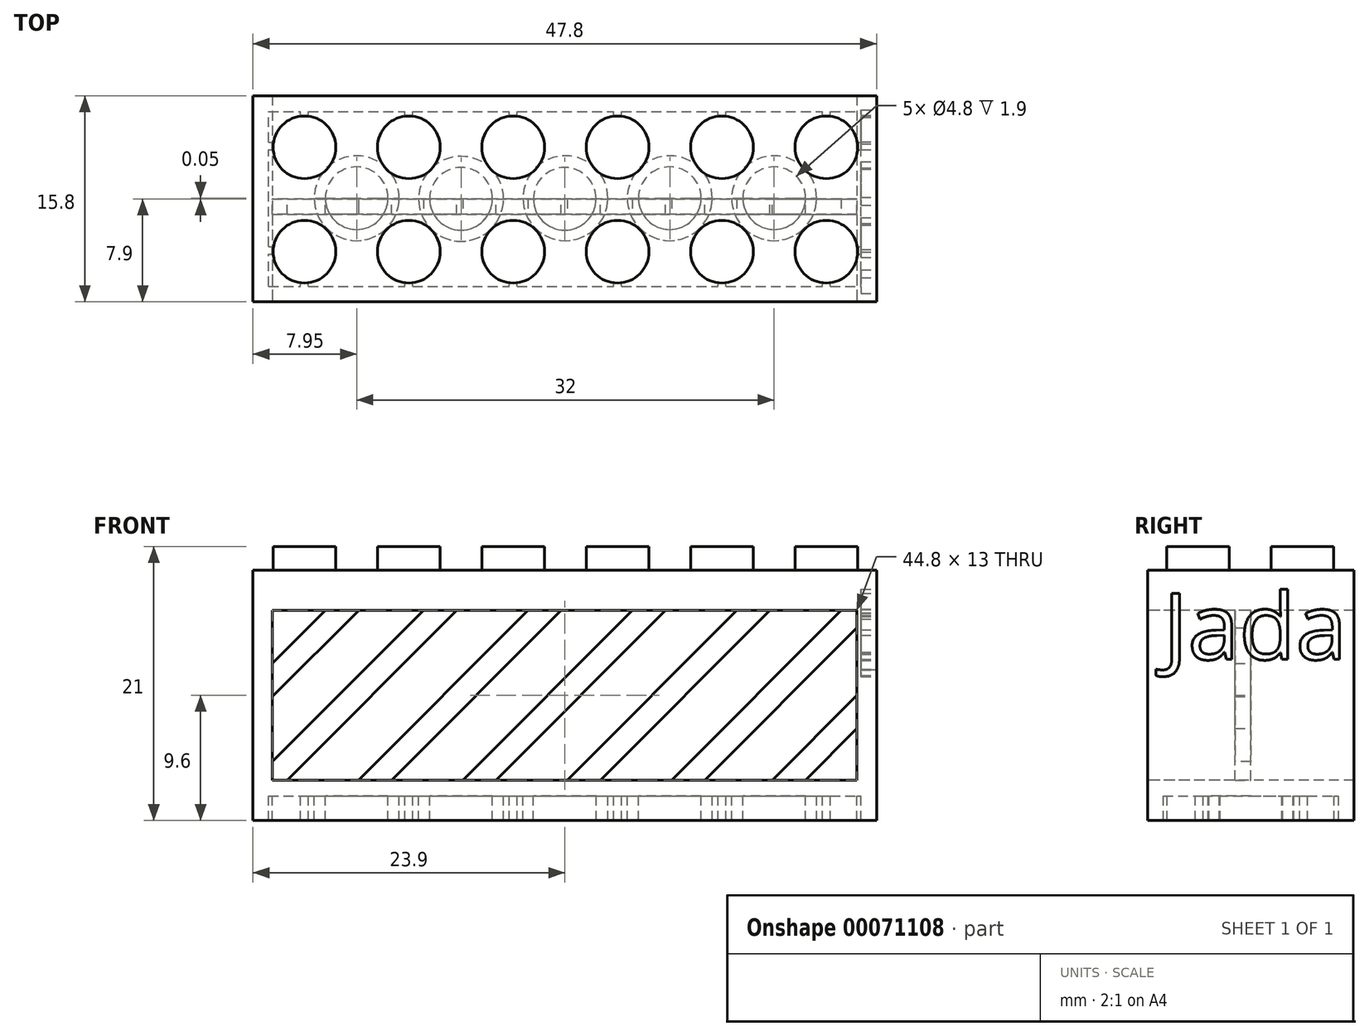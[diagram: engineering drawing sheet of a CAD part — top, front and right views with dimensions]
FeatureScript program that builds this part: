
annotation { "Feature Type Name" : "Feature", "Feature Type Description" : "" }
export const myFeature = defineFeature(function(context is Context, id is Id, definition is map)
    precondition{}
    {
        {
            var Q0;
            Q0=qCreatedBy(makeId("Top.planeOp"),FACE);
            var sketch = newSketch(context, id + "F0", { "sketchPlane" : qUnion([Q0])});
            skLineSegment(sketch, "E0.rect.bottom", {"start": v(-23.9, -7.9) * mm, "end": v(23.9, -7.9) * mm});
            skLineSegment(sketch, "E0.rect.top", {"start": v(-23.9, 7.9) * mm, "end": v(23.9, 7.9) * mm});
            skLineSegment(sketch, "E0.rect.left", {"start": v(-23.9, -7.9) * mm, "end": v(-23.9, 7.9) * mm});
            skLineSegment(sketch, "E0.rect.right", {"start": v(23.9, -7.9) * mm, "end": v(23.9, 7.9) * mm});
            skPoint(sketch, "E0.rect.middle", {"position": v(0, 0) * mm});
            skSolve(sketch);
        }
        {
            var Q0;
            Q0 = qSketchRegion(id + "F0", true);
            extrude(context, id + "F1", {"entities" : qUnion([Q0]), "depth" : 19.2 * mm});
        }
        {
            var Q0;
            Q0=makeQuery(id+"F1.opExtrude","CAP_FACE",FACE,{"disambiguationData":[OSD([sQuery(id+"F0.wireOp",EDGE,"E0.rect.bottom"),sQuery(id+"F0.wireOp",EDGE,"E0.rect.top"),sQuery(id+"F0.wireOp",EDGE,"E0.rect.left"),sQuery(id+"F0.wireOp",EDGE,"E0.rect.right")])],"isStart":true});
            var sketch = newSketch(context, id + "F2", { "sketchPlane" : qUnion([Q0])});
            skLineSegment(sketch, "E1.bottom", {"start": v(-22.7, 6.7) * mm, "end": v(22.7, 6.7) * mm});
            skLineSegment(sketch, "E1.top", {"start": v(-22.7, -6.7) * mm, "end": v(22.7, -6.7) * mm});
            skLineSegment(sketch, "E1.left", {"start": v(-22.7, 6.7) * mm, "end": v(-22.7, -6.7) * mm});
            skLineSegment(sketch, "E1.right", {"start": v(22.7, 6.7) * mm, "end": v(22.7, -6.7) * mm});
            skSolve(sketch);
        }
        {
            var Q0;
            Q0 = qSketchRegion(id + "F2", true);
            var Q1;
            Q1=makeQuery(id+"F2.imprint","IMPRINT",FACE,{"disambiguationData":[TD([[makeQuery(id+"F2.imprint","IMPRINT",EDGE,{"derivedFrom":sQuery(id+"F2.wireOp",EDGE,"E1.bottom")}),-1.0]])]});
            extrude(context, id + "F3", {"entities" : qUnion([Q0, Q1]), "operationType" : NewBodyOperationType.REMOVE, "oppositeDirection" : true, "depth" : 1.9 * mm});
        }
        {
            var Q0;
            Q0=makeQuery(id+"F1.opExtrude","SWEPT_FACE",FACE,{"disambiguationData":[OSD([sQuery(id+"F0.wireOp",EDGE,"E0.rect.bottom")])]});
            var sketch = newSketch(context, id + "F4", { "sketchPlane" : qUnion([Q0])});
            skLineSegment(sketch, "E2.bottom", {"start": v(-22.4, 16.1) * mm, "end": v(22.4, 16.1) * mm});
            skLineSegment(sketch, "E2.top", {"start": v(-22.4, 3.1) * mm, "end": v(22.4, 3.1) * mm});
            skLineSegment(sketch, "E2.left", {"start": v(-22.4, 16.1) * mm, "end": v(-22.4, 3.1) * mm});
            skLineSegment(sketch, "E2.right", {"start": v(22.4, 16.1) * mm, "end": v(22.4, 3.1) * mm});
            skSolve(sketch);
        }
        {
            var Q0;
            Q0=makeQuery(id+"F4.imprint","IMPRINT",FACE,{"disambiguationData":[TD([[makeQuery(id+"F4.imprint","IMPRINT",EDGE,{"derivedFrom":sQuery(id+"F4.wireOp",EDGE,"E2.bottom")}),-1.0]])]});
            extrude(context, id + "F5", {"entities" : qUnion([Q0]), "operationType" : NewBodyOperationType.REMOVE, "oppositeDirection" : true, "depth" : 15.8 * mm});
        }
        {
            var Q0;
            Q0=qCreatedBy(makeId("Front.planeOp"),FACE);
            var sketch = newSketch(context, id + "F6", { "sketchPlane" : qUnion([Q0])});
            skLineSegment(sketch, "E3", {"start": v(-23.8, 10.64) * mm, "end": v(-15.32, 19.12) * mm});
            skLineSegment(sketch, "E4", {"start": v(18.06, 2.72) * mm, "end": v(23.58, 8.24) * mm});
            skLineSegment(sketch, "E5", {"start": v(-23.7, 8.18) * mm, "end": v(-13.08, 18.81) * mm});
            skLineSegment(sketch, "E6", {"start": v(15.51, 2.72) * mm, "end": v(23.81, 11.02) * mm});
            skPoint(sketch, "E7", {"position": v(-15.8, 16.1) * mm});
            skPoint(sketch, "E8", {"position": v(22.4, 9.6) * mm});
            skLineSegment(sketch, "E9", {"start": v(-9.13, 17.8) * mm, "end": v(-22.8, 4.12) * mm});
            skLineSegment(sketch, "E10", {"start": v(-21.76, 2.62) * mm, "end": v(-6.76, 17.61) * mm});
            skLineSegment(sketch, "E11", {"start": v(-9.13, 17.8) * mm, "end": v(-6.76, 17.61) * mm});
            skLineSegment(sketch, "E12", {"start": v(-23.03, 2.62) * mm, "end": v(-21.76, 2.62) * mm});
            skLineSegment(sketch, "E13", {"start": v(-23.7, 8.18) * mm, "end": v(-23.8, 10.64) * mm});
            skLineSegment(sketch, "E14", {"start": v(-15.32, 19.12) * mm, "end": v(-13.08, 18.81) * mm});
            skLineSegment(sketch, "E15", {"start": v(23.58, 8.24) * mm, "end": v(23.81, 11.02) * mm});
            skLineSegment(sketch, "E16.1.0.0", {"start": v(-1.13, 17.8) * mm, "end": v(-14.8, 4.12) * mm});
            skLineSegment(sketch, "E16.1.0.1", {"start": v(-1.13, 17.8) * mm, "end": v(1.24, 17.61) * mm});
            skLineSegment(sketch, "E16.1.0.2", {"start": v(-13.76, 2.62) * mm, "end": v(1.24, 17.61) * mm});
            skLineSegment(sketch, "E16.1.0.3", {"start": v(-16.3, 2.62) * mm, "end": v(-13.76, 2.62) * mm});
            skLineSegment(sketch, "E16.1.0.4", {"start": v(-14.8, 4.12) * mm, "end": v(-16.3, 2.62) * mm});
            skLineSegment(sketch, "E16.2.0.0", {"start": v(6.87, 17.8) * mm, "end": v(-6.8, 4.12) * mm});
            skLineSegment(sketch, "E16.2.0.1", {"start": v(6.87, 17.8) * mm, "end": v(9.24, 17.61) * mm});
            skLineSegment(sketch, "E16.2.0.2", {"start": v(-5.76, 2.62) * mm, "end": v(9.24, 17.61) * mm});
            skLineSegment(sketch, "E16.2.0.3", {"start": v(-8.3, 2.62) * mm, "end": v(-5.76, 2.62) * mm});
            skLineSegment(sketch, "E16.2.0.4", {"start": v(-6.8, 4.12) * mm, "end": v(-8.3, 2.62) * mm});
            skLineSegment(sketch, "E16.3.0.0", {"start": v(14.87, 17.8) * mm, "end": v(1.2, 4.12) * mm});
            skLineSegment(sketch, "E16.3.0.1", {"start": v(14.87, 17.8) * mm, "end": v(17.24, 17.61) * mm});
            skLineSegment(sketch, "E16.3.0.2", {"start": v(2.24, 2.62) * mm, "end": v(17.24, 17.61) * mm});
            skLineSegment(sketch, "E16.3.0.3", {"start": v(-0.3, 2.62) * mm, "end": v(2.24, 2.62) * mm});
            skLineSegment(sketch, "E16.3.0.4", {"start": v(1.2, 4.12) * mm, "end": v(-0.3, 2.62) * mm});
            skLineSegment(sketch, "E16.4.0.0", {"start": v(22.87, 17.8) * mm, "end": v(9.2, 4.12) * mm});
            skLineSegment(sketch, "E16.4.0.2", {"start": v(10.24, 2.62) * mm, "end": v(23.25, 15.63) * mm});
            skLineSegment(sketch, "E16.4.0.3", {"start": v(7.7, 2.62) * mm, "end": v(10.24, 2.62) * mm});
            skLineSegment(sketch, "E16.4.0.4", {"start": v(9.2, 4.12) * mm, "end": v(7.7, 2.62) * mm});
            skLineSegment(sketch, "E16.direction1", {"start": v(-22.8, 4.12) * mm, "end": v(-14.8, 4.12) * mm, "construction": true});
            skLineSegment(sketch, "E17", {"start": v(-23.03, 2.62) * mm, "end": v(-22.8, 4.12) * mm});
            skLineSegment(sketch, "E18", {"start": v(22.87, 17.8) * mm, "end": v(23.25, 15.63) * mm});
            skLineSegment(sketch, "E19", {"start": v(15.51, 2.72) * mm, "end": v(18.06, 2.72) * mm});
            skPoint(sketch, "E20.start.orphan", {"position": v(12.8, 0) * mm});
            skPoint(sketch, "E21.orphan", {"position": v(15.34, 0) * mm});
            skSolve(sketch);
        }
        {
            var Q0;
            Q0 = qSketchRegion(id + "F6", true);
            extrude(context, id + "F7", {"entities" : qUnion([Q0]), "operationType" : NewBodyOperationType.ADD, "depth" : 1.2 * mm});
        }
        {
            var Q0;
            Q0=makeQuery(id+"F1.opExtrude","CAP_FACE",FACE,{"disambiguationData":[OSD([sQuery(id+"F0.wireOp",EDGE,"E0.rect.bottom"),sQuery(id+"F0.wireOp",EDGE,"E0.rect.top"),sQuery(id+"F0.wireOp",EDGE,"E0.rect.left"),sQuery(id+"F0.wireOp",EDGE,"E0.rect.right")])],"isStart":false});
            var sketch = newSketch(context, id + "F8", { "sketchPlane" : qUnion([Q0])});
            skCircle(sketch, "E22", {"center": v(-19.95, 3.95) * mm, "radius": 2.4 * mm});
            skCircle(sketch, "E23.0.1.0", {"center": v(-19.95, -4.05) * mm, "radius": 2.4 * mm});
            skCircle(sketch, "E23.1.0.0", {"center": v(-11.95, 3.95) * mm, "radius": 2.4 * mm});
            skCircle(sketch, "E23.1.1.0", {"center": v(-11.95, -4.05) * mm, "radius": 2.4 * mm});
            skCircle(sketch, "E23.2.0.0", {"center": v(-3.95, 3.95) * mm, "radius": 2.4 * mm});
            skCircle(sketch, "E23.2.1.0", {"center": v(-3.95, -4.05) * mm, "radius": 2.4 * mm});
            skCircle(sketch, "E23.3.0.0", {"center": v(4.05, 3.95) * mm, "radius": 2.4 * mm});
            skCircle(sketch, "E23.3.1.0", {"center": v(4.05, -4.05) * mm, "radius": 2.4 * mm});
            skCircle(sketch, "E23.4.0.0", {"center": v(12.05, 3.95) * mm, "radius": 2.4 * mm});
            skCircle(sketch, "E23.4.1.0", {"center": v(12.05, -4.05) * mm, "radius": 2.4 * mm});
            skCircle(sketch, "E23.5.0.0", {"center": v(20.05, 3.95) * mm, "radius": 2.4 * mm});
            skCircle(sketch, "E23.5.1.0", {"center": v(20.05, -4.05) * mm, "radius": 2.4 * mm});
            skLineSegment(sketch, "E23.direction1", {"start": v(-19.95, 3.95) * mm, "end": v(-11.95, 3.95) * mm, "construction": true});
            skLineSegment(sketch, "E23.direction2", {"start": v(-19.95, 3.95) * mm, "end": v(-19.95, -4.05) * mm, "construction": true});
            skSolve(sketch);
        }
        {
            var Q0;
            Q0 = qSketchRegion(id + "F8", true);
            extrude(context, id + "F9", {"entities" : qUnion([Q0]), "operationType" : NewBodyOperationType.ADD, "depth" : 1.8 * mm});
        }
        {
            var Q0;
            Q0=makeQuery(id+"F3.boolean.opBoolean","COPY",FACE,{"derivedFrom":makeQuery(id+"F3.opExtrude","CAP_FACE",FACE,{"disambiguationData":[OSD([sQuery(id+"F2.wireOp",EDGE,"E1.bottom"),sQuery(id+"F2.wireOp",EDGE,"E1.top"),sQuery(id+"F2.wireOp",EDGE,"E1.left"),sQuery(id+"F2.wireOp",EDGE,"E1.right")])],"isStart":false})});
            var sketch = newSketch(context, id + "F10", { "sketchPlane" : qUnion([Q0])});
            skCircle(sketch, "E24", {"center": v(-19.95, 3.95) * mm, "radius": 1.3 * mm, "construction": true});
            skCircle(sketch, "E25.0.1.0", {"center": v(-19.95, -4.05) * mm, "radius": 1.3 * mm, "construction": true});
            skCircle(sketch, "E25.1.0.0", {"center": v(-11.95, 3.95) * mm, "radius": 1.3 * mm, "construction": true});
            skCircle(sketch, "E25.1.1.0", {"center": v(-11.95, -4.05) * mm, "radius": 1.3 * mm, "construction": true});
            skCircle(sketch, "E25.2.0.0", {"center": v(-3.95, 3.95) * mm, "radius": 1.3 * mm, "construction": true});
            skCircle(sketch, "E25.2.1.0", {"center": v(-3.95, -4.05) * mm, "radius": 1.3 * mm, "construction": true});
            skCircle(sketch, "E25.3.0.0", {"center": v(4.05, 3.95) * mm, "radius": 1.3 * mm, "construction": true});
            skCircle(sketch, "E25.3.1.0", {"center": v(4.05, -4.05) * mm, "radius": 1.3 * mm, "construction": true});
            skCircle(sketch, "E25.4.0.0", {"center": v(12.05, 3.95) * mm, "radius": 1.3 * mm, "construction": true});
            skCircle(sketch, "E25.4.1.0", {"center": v(12.05, -4.05) * mm, "radius": 1.3 * mm, "construction": true});
            skCircle(sketch, "E25.5.0.0", {"center": v(20.05, 3.95) * mm, "radius": 1.3 * mm, "construction": true});
            skCircle(sketch, "E25.5.1.0", {"center": v(20.05, -4.05) * mm, "radius": 1.3 * mm, "construction": true});
            skLineSegment(sketch, "E25.direction1", {"start": v(-19.95, 3.95) * mm, "end": v(-11.95, 3.95) * mm, "construction": true});
            skLineSegment(sketch, "E25.direction2", {"start": v(-19.95, 3.95) * mm, "end": v(-19.95, -4.05) * mm, "construction": true});
            skLineSegment(sketch, "E26", {"start": v(-11.95, 3.95) * mm, "end": v(-19.95, -4.05) * mm, "construction": true});
            skLineSegment(sketch, "E27", {"start": v(-11.95, 3.95) * mm, "end": v(-3.95, -4.05) * mm, "construction": true});
            skLineSegment(sketch, "E28", {"start": v(4.05, 3.95) * mm, "end": v(-3.95, -4.05) * mm, "construction": true});
            skLineSegment(sketch, "E29", {"start": v(4.05, 3.95) * mm, "end": v(12.05, -4.05) * mm, "construction": true});
            skLineSegment(sketch, "E30", {"start": v(20.05, 3.95) * mm, "end": v(12.05, -4.05) * mm, "construction": true});
            skLineSegment(sketch, "E31", {"start": v(20.05, -4.05) * mm, "end": v(12.05, 3.95) * mm, "construction": true});
            skLineSegment(sketch, "E32", {"start": v(12.05, 3.95) * mm, "end": v(4.05, -4.05) * mm, "construction": true});
            skLineSegment(sketch, "E33", {"start": v(4.05, -4.05) * mm, "end": v(-3.95, 3.95) * mm, "construction": true});
            skLineSegment(sketch, "E34", {"start": v(-3.95, 3.95) * mm, "end": v(-11.95, -4.05) * mm, "construction": true});
            skLineSegment(sketch, "E35", {"start": v(-11.95, -4.05) * mm, "end": v(-19.95, 3.95) * mm, "construction": true});
            skPoint(sketch, "E36", {"position": v(8.05, -0.05) * mm});
            skPoint(sketch, "E37", {"position": v(16.05, -0.05) * mm});
            skPoint(sketch, "E38", {"position": v(0.05, -0.05) * mm});
            skPoint(sketch, "E39", {"position": v(-7.95, 0) * mm});
            skPoint(sketch, "E39.positionSnap0", {"position": v(-7.95, -0.05) * mm});
            skPoint(sketch, "E40", {"position": v(-15.95, -0.05) * mm});
            skCircle(sketch, "E41", {"center": v(16.05, -0.05) * mm, "radius": 3.25 * mm});
            skCircle(sketch, "E42", {"center": v(8.05, -0.05) * mm, "radius": 3.25 * mm});
            skCircle(sketch, "E43", {"center": v(0.05, -0.05) * mm, "radius": 3.25 * mm});
            skCircle(sketch, "E44", {"center": v(-7.95, 0) * mm, "radius": 3.25 * mm});
            skCircle(sketch, "E45", {"center": v(-15.95, -0.05) * mm, "radius": 3.25 * mm});
            skCircle(sketch, "E46", {"center": v(16.05, -0.05) * mm, "radius": 2.4 * mm});
            skCircle(sketch, "E47", {"center": v(8.05, -0.05) * mm, "radius": 2.4 * mm});
            skCircle(sketch, "E48", {"center": v(0, 0) * mm, "radius": 2.4 * mm});
            skCircle(sketch, "E49", {"center": v(-7.95, 0) * mm, "radius": 2.4 * mm});
            skCircle(sketch, "E50", {"center": v(-15.95, -0.05) * mm, "radius": 2.4 * mm});
            skSolve(sketch);
        }
        {
            var Q0;
            Q0 = qSketchRegion(id + "F10", true);
            var Q1;
            Q1=makeQuery(id+"F1.opExtrude","CAP_FACE",FACE,{"disambiguationData":[OSD([sQuery(id+"F0.wireOp",EDGE,"E0.rect.bottom"),sQuery(id+"F0.wireOp",EDGE,"E0.rect.top"),sQuery(id+"F0.wireOp",EDGE,"E0.rect.left"),sQuery(id+"F0.wireOp",EDGE,"E0.rect.right")])],"isStart":true});
            extrude(context, id + "F11", {"entities" : qUnion([Q0]), "operationType" : NewBodyOperationType.ADD, "endBound" : BoundingType.UP_TO_SURFACE, "endBoundEntityFace" : qUnion([Q1]), "depth" : 25 * mm});
        }
        {
            var Q0;
            {var subQ0=sQuery(id+"F2.wireOp",EDGE,"E1.right");var subQ1=sQuery(id+"F2.wireOp",EDGE,"E1.left");var subQ2=sQuery(id+"F2.wireOp",EDGE,"E1.top");var subQ3=sQuery(id+"F2.wireOp",EDGE,"E1.bottom");Q0=makeQuery(id+"F11.boolean.opBoolean","SPLIT",FACE,{"disambiguationData":[TD([makeQuery(id+"F3.boolean.opBoolean","COPY",FACE,{"derivedFrom":makeQuery(id+"F3.opExtrude","SWEPT_FACE",FACE,{"disambiguationData":[OSD([subQ3])]})})])],"derivedFrom":makeQuery(id+"F3.boolean.opBoolean","COPY",FACE,{"derivedFrom":makeQuery(id+"F3.opExtrude","CAP_FACE",FACE,{"disambiguationData":[OSD([subQ3,subQ2,subQ1,subQ0])],"isStart":false})})});}
            var sketch = newSketch(context, id + "F12", { "sketchPlane" : qUnion([Q0])});
            skLineSegment(sketch, "E51", {"start": v(-19.95, -4.05) * mm, "end": v(-19.95, 13.37) * mm, "construction": true});
            skLineSegment(sketch, "E52.bottom", {"start": v(-20.25, 6.7) * mm, "end": v(-19.65, 6.7) * mm});
            skLineSegment(sketch, "E52.top", {"start": v(-20.25, 6.4) * mm, "end": v(-19.65, 6.4) * mm});
            skLineSegment(sketch, "E52.left", {"start": v(-20.25, 6.7) * mm, "end": v(-20.25, 6.4) * mm});
            skLineSegment(sketch, "E52.right", {"start": v(-19.65, 6.7) * mm, "end": v(-19.65, 6.4) * mm});
            skLineSegment(sketch, "E53.0.1.0", {"start": v(-19.65, -6.4) * mm, "end": v(-19.65, -6.7) * mm});
            skLineSegment(sketch, "E53.0.1.1", {"start": v(-20.25, -6.7) * mm, "end": v(-19.65, -6.7) * mm});
            skLineSegment(sketch, "E53.0.1.2", {"start": v(-20.25, -6.4) * mm, "end": v(-20.25, -6.7) * mm});
            skLineSegment(sketch, "E53.0.1.3", {"start": v(-20.25, -6.4) * mm, "end": v(-19.65, -6.4) * mm});
            skLineSegment(sketch, "E53.1.0.0", {"start": v(-11.65, 6.7) * mm, "end": v(-11.65, 6.4) * mm});
            skLineSegment(sketch, "E53.1.0.1", {"start": v(-12.25, 6.4) * mm, "end": v(-11.65, 6.4) * mm});
            skLineSegment(sketch, "E53.1.0.2", {"start": v(-12.25, 6.7) * mm, "end": v(-12.25, 6.4) * mm});
            skLineSegment(sketch, "E53.1.0.3", {"start": v(-12.25, 6.7) * mm, "end": v(-11.65, 6.7) * mm});
            skLineSegment(sketch, "E53.1.1.0", {"start": v(-11.65, -6.4) * mm, "end": v(-11.65, -6.7) * mm});
            skLineSegment(sketch, "E53.1.1.1", {"start": v(-12.25, -6.7) * mm, "end": v(-11.65, -6.7) * mm});
            skLineSegment(sketch, "E53.1.1.2", {"start": v(-12.25, -6.4) * mm, "end": v(-12.25, -6.7) * mm});
            skLineSegment(sketch, "E53.1.1.3", {"start": v(-12.25, -6.4) * mm, "end": v(-11.65, -6.4) * mm});
            skLineSegment(sketch, "E53.2.0.0", {"start": v(-3.65, 6.7) * mm, "end": v(-3.65, 6.4) * mm});
            skLineSegment(sketch, "E53.2.0.1", {"start": v(-4.25, 6.4) * mm, "end": v(-3.65, 6.4) * mm});
            skLineSegment(sketch, "E53.2.0.2", {"start": v(-4.25, 6.7) * mm, "end": v(-4.25, 6.4) * mm});
            skLineSegment(sketch, "E53.2.0.3", {"start": v(-4.25, 6.7) * mm, "end": v(-3.65, 6.7) * mm});
            skLineSegment(sketch, "E53.2.1.0", {"start": v(-3.65, -6.4) * mm, "end": v(-3.65, -6.7) * mm});
            skLineSegment(sketch, "E53.2.1.1", {"start": v(-4.25, -6.7) * mm, "end": v(-3.65, -6.7) * mm});
            skLineSegment(sketch, "E53.2.1.2", {"start": v(-4.25, -6.4) * mm, "end": v(-4.25, -6.7) * mm});
            skLineSegment(sketch, "E53.2.1.3", {"start": v(-4.25, -6.4) * mm, "end": v(-3.65, -6.4) * mm});
            skLineSegment(sketch, "E53.3.0.0", {"start": v(4.35, 6.7) * mm, "end": v(4.35, 6.4) * mm});
            skLineSegment(sketch, "E53.3.0.1", {"start": v(3.75, 6.4) * mm, "end": v(4.35, 6.4) * mm});
            skLineSegment(sketch, "E53.3.0.2", {"start": v(3.75, 6.7) * mm, "end": v(3.75, 6.4) * mm});
            skLineSegment(sketch, "E53.3.0.3", {"start": v(3.75, 6.7) * mm, "end": v(4.35, 6.7) * mm});
            skLineSegment(sketch, "E53.3.1.0", {"start": v(4.35, -6.4) * mm, "end": v(4.35, -6.7) * mm});
            skLineSegment(sketch, "E53.3.1.1", {"start": v(3.75, -6.7) * mm, "end": v(4.35, -6.7) * mm});
            skLineSegment(sketch, "E53.3.1.2", {"start": v(3.75, -6.4) * mm, "end": v(3.75, -6.7) * mm});
            skLineSegment(sketch, "E53.3.1.3", {"start": v(3.75, -6.4) * mm, "end": v(4.35, -6.4) * mm});
            skLineSegment(sketch, "E53.4.0.0", {"start": v(12.35, 6.7) * mm, "end": v(12.35, 6.4) * mm});
            skLineSegment(sketch, "E53.4.0.1", {"start": v(11.75, 6.4) * mm, "end": v(12.35, 6.4) * mm});
            skLineSegment(sketch, "E53.4.0.2", {"start": v(11.75, 6.7) * mm, "end": v(11.75, 6.4) * mm});
            skLineSegment(sketch, "E53.4.0.3", {"start": v(11.75, 6.7) * mm, "end": v(12.35, 6.7) * mm});
            skLineSegment(sketch, "E53.4.1.0", {"start": v(12.35, -6.4) * mm, "end": v(12.35, -6.7) * mm});
            skLineSegment(sketch, "E53.4.1.1", {"start": v(11.75, -6.7) * mm, "end": v(12.35, -6.7) * mm});
            skLineSegment(sketch, "E53.4.1.2", {"start": v(11.75, -6.4) * mm, "end": v(11.75, -6.7) * mm});
            skLineSegment(sketch, "E53.4.1.3", {"start": v(11.75, -6.4) * mm, "end": v(12.35, -6.4) * mm});
            skLineSegment(sketch, "E53.5.0.0", {"start": v(20.35, 6.7) * mm, "end": v(20.35, 6.4) * mm});
            skLineSegment(sketch, "E53.5.0.1", {"start": v(19.75, 6.4) * mm, "end": v(20.35, 6.4) * mm});
            skLineSegment(sketch, "E53.5.0.2", {"start": v(19.75, 6.7) * mm, "end": v(19.75, 6.4) * mm});
            skLineSegment(sketch, "E53.5.0.3", {"start": v(19.75, 6.7) * mm, "end": v(20.35, 6.7) * mm});
            skLineSegment(sketch, "E53.5.1.0", {"start": v(20.35, -6.4) * mm, "end": v(20.35, -6.7) * mm});
            skLineSegment(sketch, "E53.5.1.1", {"start": v(19.75, -6.7) * mm, "end": v(20.35, -6.7) * mm});
            skLineSegment(sketch, "E53.5.1.2", {"start": v(19.75, -6.4) * mm, "end": v(19.75, -6.7) * mm});
            skLineSegment(sketch, "E53.5.1.3", {"start": v(19.75, -6.4) * mm, "end": v(20.35, -6.4) * mm});
            skLineSegment(sketch, "E53.direction1", {"start": v(-19.65, 6.4) * mm, "end": v(-11.65, 6.4) * mm, "construction": true});
            skLineSegment(sketch, "E53.direction2", {"start": v(-19.65, 6.4) * mm, "end": v(-19.65, -6.7) * mm, "construction": true});
            skSolve(sketch);
        }
        {
            var Q0;
            Q0=makeQuery(id+"F10.imprint","IMPRINT",FACE,{"disambiguationData":[TD([[makeQuery(id+"F10.imprint","IMPRINT",EDGE,{"derivedFrom":sQuery(id+"F10.wireOp",EDGE,"E41")}),-1.0]])]});
            var sketch = newSketch(context, id + "F13", { "sketchPlane" : qUnion([Q0])});
            skSolve(sketch);
        }
        {
            var Q0;
            Q0 = qSketchRegion(id + "F12", true);
            var Q1;
            Q1=makeQuery(id+"F1.opExtrude","CAP_FACE",FACE,{"disambiguationData":[OSD([sQuery(id+"F0.wireOp",EDGE,"E0.rect.bottom"),sQuery(id+"F0.wireOp",EDGE,"E0.rect.top"),sQuery(id+"F0.wireOp",EDGE,"E0.rect.left"),sQuery(id+"F0.wireOp",EDGE,"E0.rect.right")])],"isStart":true});
            extrude(context, id + "F14", {"entities" : qUnion([Q0]), "operationType" : NewBodyOperationType.ADD, "endBound" : BoundingType.UP_TO_SURFACE, "endBoundEntityFace" : qUnion([Q1]), "depth" : 25 * mm});
        }
        {
            var Q0;
            Q0=makeQuery(id+"F10.imprint","IMPRINT",FACE,{"disambiguationData":[TD([[makeQuery(id+"F10.imprint","IMPRINT",EDGE,{"derivedFrom":sQuery(id+"F10.wireOp",EDGE,"E41")}),-1.0]])]});
            var sketch = newSketch(context, id + "F15", { "sketchPlane" : qUnion([Q0])});
            skLineSegment(sketch, "E54.bottom", {"start": v(-22.7, 4.25) * mm, "end": v(-22.4, 4.25) * mm});
            skLineSegment(sketch, "E54.top", {"start": v(-22.7, 3.65) * mm, "end": v(-22.4, 3.65) * mm});
            skLineSegment(sketch, "E54.left", {"start": v(-22.7, 4.25) * mm, "end": v(-22.7, 3.65) * mm});
            skLineSegment(sketch, "E54.right", {"start": v(-22.4, 4.25) * mm, "end": v(-22.4, 3.65) * mm});
            skLineSegment(sketch, "E55", {"start": v(-11.95, 3.95) * mm, "end": v(-25.4, 3.95) * mm, "construction": true});
            skLineSegment(sketch, "E56.0.1.0", {"start": v(-22.7, -3.75) * mm, "end": v(-22.4, -3.75) * mm});
            skLineSegment(sketch, "E56.0.1.1", {"start": v(-22.4, -3.75) * mm, "end": v(-22.4, -4.35) * mm});
            skLineSegment(sketch, "E56.0.1.2", {"start": v(-22.7, -4.35) * mm, "end": v(-22.4, -4.35) * mm});
            skLineSegment(sketch, "E56.0.1.3", {"start": v(-22.7, -3.75) * mm, "end": v(-22.7, -4.35) * mm});
            skLineSegment(sketch, "E56.1.0.0", {"start": v(22.4, 4.25) * mm, "end": v(22.7, 4.25) * mm});
            skLineSegment(sketch, "E56.1.0.1", {"start": v(22.7, 4.25) * mm, "end": v(22.7, 3.65) * mm});
            skLineSegment(sketch, "E56.1.0.2", {"start": v(22.4, 3.65) * mm, "end": v(22.7, 3.65) * mm});
            skLineSegment(sketch, "E56.1.0.3", {"start": v(22.4, 4.25) * mm, "end": v(22.4, 3.65) * mm});
            skLineSegment(sketch, "E56.1.1.0", {"start": v(22.4, -3.75) * mm, "end": v(22.7, -3.75) * mm});
            skLineSegment(sketch, "E56.1.1.1", {"start": v(22.7, -3.75) * mm, "end": v(22.7, -4.35) * mm});
            skLineSegment(sketch, "E56.1.1.2", {"start": v(22.4, -4.35) * mm, "end": v(22.7, -4.35) * mm});
            skLineSegment(sketch, "E56.1.1.3", {"start": v(22.4, -3.75) * mm, "end": v(22.4, -4.35) * mm});
            skLineSegment(sketch, "E56.direction1", {"start": v(-22.7, 4.25) * mm, "end": v(22.4, 4.25) * mm, "construction": true});
            skLineSegment(sketch, "E56.direction2", {"start": v(-22.7, 4.25) * mm, "end": v(-22.7, -3.75) * mm, "construction": true});
            skSolve(sketch);
        }
        {
            var Q0;
            Q0 = qSketchRegion(id + "F15", true);
            var Q1;
            Q1=makeQuery(id+"F14.boolean.opBoolean","MERGE",FACE,{"derivedFrom":[makeQuery(id+"F1.opExtrude","CAP_FACE",FACE,{"disambiguationData":[OSD([sQuery(id+"F0.wireOp",EDGE,"E0.rect.bottom"),sQuery(id+"F0.wireOp",EDGE,"E0.rect.top"),sQuery(id+"F0.wireOp",EDGE,"E0.rect.left"),sQuery(id+"F0.wireOp",EDGE,"E0.rect.right")])],"isStart":true}),makeQuery(id+"F14.opExtrude","CAP_FACE",FACE,{"disambiguationData":[OSD([sQuery(id+"F12.wireOp",EDGE,"E52.bottom"),sQuery(id+"F12.wireOp",EDGE,"E52.top"),sQuery(id+"F12.wireOp",EDGE,"E52.left"),sQuery(id+"F12.wireOp",EDGE,"E52.right")])],"isStart":false}),makeQuery(id+"F14.opExtrude","CAP_FACE",FACE,{"disambiguationData":[OSD([sQuery(id+"F12.wireOp",EDGE,"E53.0.1.0"),sQuery(id+"F12.wireOp",EDGE,"E53.0.1.1"),sQuery(id+"F12.wireOp",EDGE,"E53.0.1.2"),sQuery(id+"F12.wireOp",EDGE,"E53.0.1.3")])],"isStart":false}),makeQuery(id+"F14.opExtrude","CAP_FACE",FACE,{"disambiguationData":[OSD([sQuery(id+"F12.wireOp",EDGE,"E53.1.0.0"),sQuery(id+"F12.wireOp",EDGE,"E53.1.0.1"),sQuery(id+"F12.wireOp",EDGE,"E53.1.0.2"),sQuery(id+"F12.wireOp",EDGE,"E53.1.0.3")])],"isStart":false}),makeQuery(id+"F14.opExtrude","CAP_FACE",FACE,{"disambiguationData":[OSD([sQuery(id+"F12.wireOp",EDGE,"E53.1.1.0"),sQuery(id+"F12.wireOp",EDGE,"E53.1.1.1"),sQuery(id+"F12.wireOp",EDGE,"E53.1.1.2"),sQuery(id+"F12.wireOp",EDGE,"E53.1.1.3")])],"isStart":false}),makeQuery(id+"F14.opExtrude","CAP_FACE",FACE,{"disambiguationData":[OSD([sQuery(id+"F12.wireOp",EDGE,"E53.2.0.0"),sQuery(id+"F12.wireOp",EDGE,"E53.2.0.1"),sQuery(id+"F12.wireOp",EDGE,"E53.2.0.2"),sQuery(id+"F12.wireOp",EDGE,"E53.2.0.3")])],"isStart":false}),makeQuery(id+"F14.opExtrude","CAP_FACE",FACE,{"disambiguationData":[OSD([sQuery(id+"F12.wireOp",EDGE,"E53.2.1.0"),sQuery(id+"F12.wireOp",EDGE,"E53.2.1.1"),sQuery(id+"F12.wireOp",EDGE,"E53.2.1.2"),sQuery(id+"F12.wireOp",EDGE,"E53.2.1.3")])],"isStart":false}),makeQuery(id+"F14.opExtrude","CAP_FACE",FACE,{"disambiguationData":[OSD([sQuery(id+"F12.wireOp",EDGE,"E53.3.0.0"),sQuery(id+"F12.wireOp",EDGE,"E53.3.0.1"),sQuery(id+"F12.wireOp",EDGE,"E53.3.0.2"),sQuery(id+"F12.wireOp",EDGE,"E53.3.0.3")])],"isStart":false}),makeQuery(id+"F14.opExtrude","CAP_FACE",FACE,{"disambiguationData":[OSD([sQuery(id+"F12.wireOp",EDGE,"E53.3.1.0"),sQuery(id+"F12.wireOp",EDGE,"E53.3.1.1"),sQuery(id+"F12.wireOp",EDGE,"E53.3.1.2"),sQuery(id+"F12.wireOp",EDGE,"E53.3.1.3")])],"isStart":false}),makeQuery(id+"F14.opExtrude","CAP_FACE",FACE,{"disambiguationData":[OSD([sQuery(id+"F12.wireOp",EDGE,"E53.4.0.0"),sQuery(id+"F12.wireOp",EDGE,"E53.4.0.1"),sQuery(id+"F12.wireOp",EDGE,"E53.4.0.2"),sQuery(id+"F12.wireOp",EDGE,"E53.4.0.3")])],"isStart":false}),makeQuery(id+"F14.opExtrude","CAP_FACE",FACE,{"disambiguationData":[OSD([sQuery(id+"F12.wireOp",EDGE,"E53.4.1.0"),sQuery(id+"F12.wireOp",EDGE,"E53.4.1.1"),sQuery(id+"F12.wireOp",EDGE,"E53.4.1.2"),sQuery(id+"F12.wireOp",EDGE,"E53.4.1.3")])],"isStart":false}),makeQuery(id+"F14.opExtrude","CAP_FACE",FACE,{"disambiguationData":[OSD([sQuery(id+"F12.wireOp",EDGE,"E53.5.0.0"),sQuery(id+"F12.wireOp",EDGE,"E53.5.0.1"),sQuery(id+"F12.wireOp",EDGE,"E53.5.0.2"),sQuery(id+"F12.wireOp",EDGE,"E53.5.0.3")])],"isStart":false}),makeQuery(id+"F14.opExtrude","CAP_FACE",FACE,{"disambiguationData":[OSD([sQuery(id+"F12.wireOp",EDGE,"E53.5.1.0"),sQuery(id+"F12.wireOp",EDGE,"E53.5.1.1"),sQuery(id+"F12.wireOp",EDGE,"E53.5.1.2"),sQuery(id+"F12.wireOp",EDGE,"E53.5.1.3")])],"isStart":false})]});
            extrude(context, id + "F16", {"entities" : qUnion([Q0]), "operationType" : NewBodyOperationType.ADD, "endBound" : BoundingType.UP_TO_SURFACE, "endBoundEntityFace" : qUnion([Q1]), "depth" : 25 * mm});
        }
        {
            var Q0;
            Q0=makeQuery(id+"F1.opExtrude","SWEPT_FACE",FACE,{"disambiguationData":[OSD([sQuery(id+"F0.wireOp",EDGE,"E0.rect.right")])]});
            var sketch = newSketch(context, id + "F17", { "sketchPlane" : qUnion([Q0])});
            skText(sketch, "E57", { "text": "Jada", "fontName": "OpenSans-Regular.ttf"});
            const initialGuessF17  = {"E57": [-0.0067, 0.01235, 1, 0, 0.00509]};
            skSetInitialGuess(sketch, initialGuessF17);
            skSolve(sketch);
        }
        {
            var Q0;
            Q0 = qSketchRegion(id + "F17", true);
            extrude(context, id + "F18", {"entities" : qUnion([Q0]), "operationType" : NewBodyOperationType.REMOVE, "oppositeDirection" : true, "depth" : 1.2 * mm});
        }
    });
